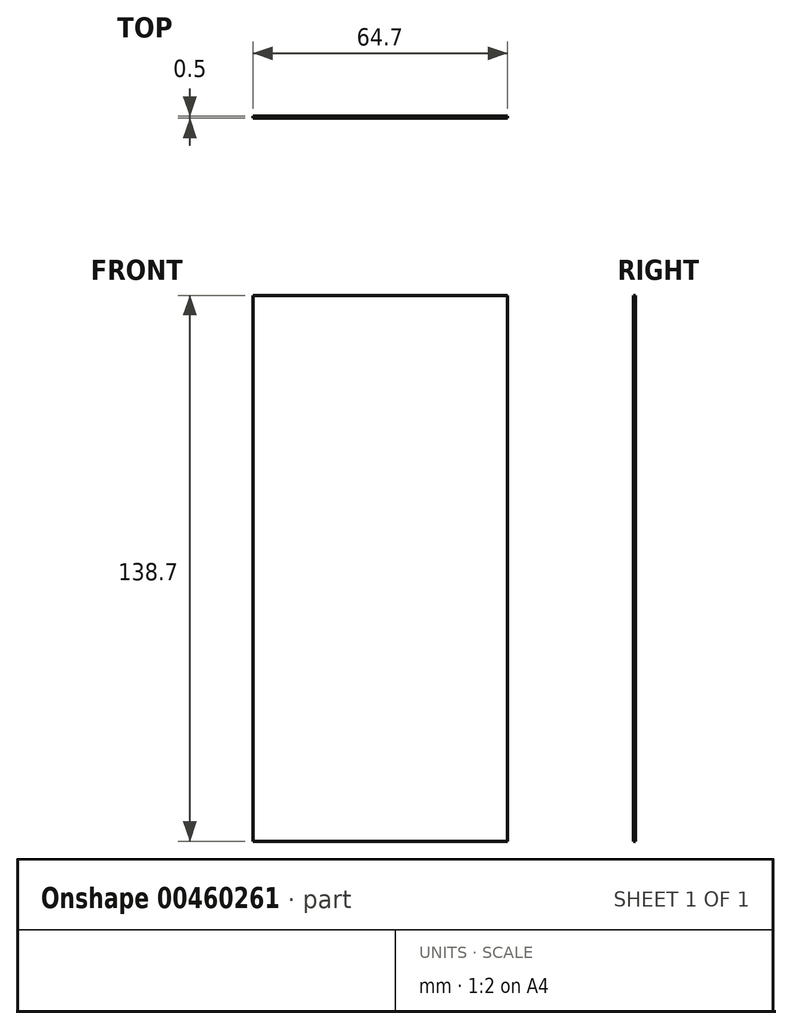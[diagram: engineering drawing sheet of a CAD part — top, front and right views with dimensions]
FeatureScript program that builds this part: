
annotation { "Feature Type Name" : "Feature", "Feature Type Description" : "" }
export const myFeature = defineFeature(function(context is Context, id is Id, definition is map)
    precondition{}
    {
        {
            var Q0;
            Q0=qCreatedBy(makeId("Front.planeOp"),FACE);
            var sketch = newSketch(context, id + "F0", { "sketchPlane" : qUnion([Q0])});
            skLineSegment(sketch, "E0", {"start": v(-32.35, 69.35) * mm, "end": v(32.35, 69.35) * mm});
            skLineSegment(sketch, "E1", {"start": v(32.35, 69.35) * mm, "end": v(32.35, -69.35) * mm});
            skLineSegment(sketch, "E2", {"start": v(32.35, -69.35) * mm, "end": v(-32.35, -69.35) * mm});
            skLineSegment(sketch, "E3", {"start": v(-32.35, -69.35) * mm, "end": v(-32.35, 69.35) * mm});
            skSolve(sketch);
        }
        {
            var Q0;
            Q0=qSketchRegion(id+"F0",true);
            extrude(context, id + "F1", {"entities" : qUnion([Q0]), "depth" : 2 * mm});
        }
        {
            var Q0;
            Q0=makeQuery(id+"F1.opExtrude","CAP_FACE",FACE,{"disambiguationData":[OSD([sQuery(id+"F0.wireOp",EDGE,"E0"),sQuery(id+"F0.wireOp",EDGE,"E1"),sQuery(id+"F0.wireOp",EDGE,"E2"),sQuery(id+"F0.wireOp",EDGE,"E3")])],"isStart":true});
            extrude(context, id + "F2", {"entities" : qUnion([Q0]), "operationType" : NewBodyOperationType.REMOVE, "oppositeDirection" : true, "depth" : 1.5 * mm});
        }
    });
